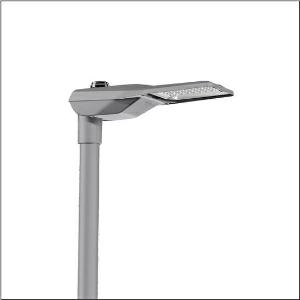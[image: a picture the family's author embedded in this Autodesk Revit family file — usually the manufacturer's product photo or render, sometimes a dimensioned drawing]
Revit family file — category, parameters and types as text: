
# Revit family: streetlight_sl_21_mini___st1_0a_5xe6d27n08jb_0e68
name_source: partatom
category: Lighting Fixtures
units: mm (PartAtom-declared; Revit-internal decimal feet)

## family parameters
Cut with Voids When Loaded = No
Host = Face
Light Source = No
Part Type = Normal
Room Calculation Point = No
Round Connector Dimension = Use Diameter
Shared = No

## types (1)
- --- (1 x LED, 10620 lm, 87.3 W, 2200K)
    Apparent Load = 87 VA
    CIE Flux Codes = 40 73 97 100 100
    Color Rendering = 70
    Color Temperature = 2200K
    Default Elevation = 1800 mm
    Description = Streetlight SL 21 mini, mast luminaire, primary light control with lens, of PMMA, primary optical cover: cover, of toughened safety glass, transparent, light distribution: ST1.0a, light emission: direct distribution, primary light characteristic: asymmetric, installation type: side-entry, LED, 3G 2.5mm², High Power LED, rated luminous flux: 10.620lm, luminous efficacy: 122lm/W, light colour: 722, colour temperature: 2200K, control: overheat protection, pre-setting: linear dimming characteristic, constant luminous flux control, time-dependent luminous flux control, flexible luminous flux parameterisation, mains connection: 230..240V, AC, 50/60Hz, connection cable pre-assembled, cable length: 10,5m, wiring characteristics: H05VV-F, start of lifetime: 87W, end of service life: 90W, reduction: 40W, luminaire housing, of diecast aluminium (EN AC-44300), powder-coated, Siteco® metallic grey (DB 702S), corrosivity category C5 mid according to DIN EN ISO 12944, multi-level sealing system, sealing non-destructively replaceable, inclination adjustable: 0°, 5°, 10°, 15°, length: 628mm, width: 235mm, height: 110mm, spigot size: 42mm (side-entry), protection rating (complete): IP66, insulation class (complete): insulation class I (protective earthing), certification: CE, ENEC, ENEC+, VDE, impact resistance: IK09, permissible operating ambient temperature for outdoor applications: -40..+50°C, standard-compliant lighting for roads and squares, packaging unit: 1 piece

Light Distribution: ST1.0a
    Height = 110 mm
    Lamp = 1 x LED
    Lamp Light Flux = 10620 lm
    Lamp Power = 87.3 W
    Lamp count = 1
    Length = 625 mm
    Luminous efficacy = 122 lm/W
    Manufacturer = Siteco
    ModVariant = No
    Model = 5XE6D27N08JB
    Number of Poles = 1
    OnlyDefault = Yes
    Power Factor = 1
    Product Name = Streetlight SL 21 mini | ST1.0a
    Product group = mast luminaire | pylon top
    ProductGroupID = 6100
    Protection Class = Protection class I
    Protection Degree = IP 66
    RLX_Detail_Level = 1
    RLX_Emergency_Light_Flux = 0 lm
    RLX_Emergency_Type = 0
    RLX_Emergency_Type_DB = No
    RlxData = <blob elided: 91645 chars, md5=266d18b5>
    Socket = socket
    Standby Power = 0 W
    System Light Flux = 10620 lm
    System Power = 87 W
    Type Comments = factory setting: luminous flux: 100 % | dim-lin: 254 | 915 mA
    Type Image = l_1294379.jpg
    URL = http://relux.com
    VarID = @adj_105205
    Voltage = 0 V
    Weight = 0.00 kg
    Width = 234 mm

## geometry (parser evidence)
native form markers: Blend x4, Sweep x11
no freeform markers — native parametric forms only
